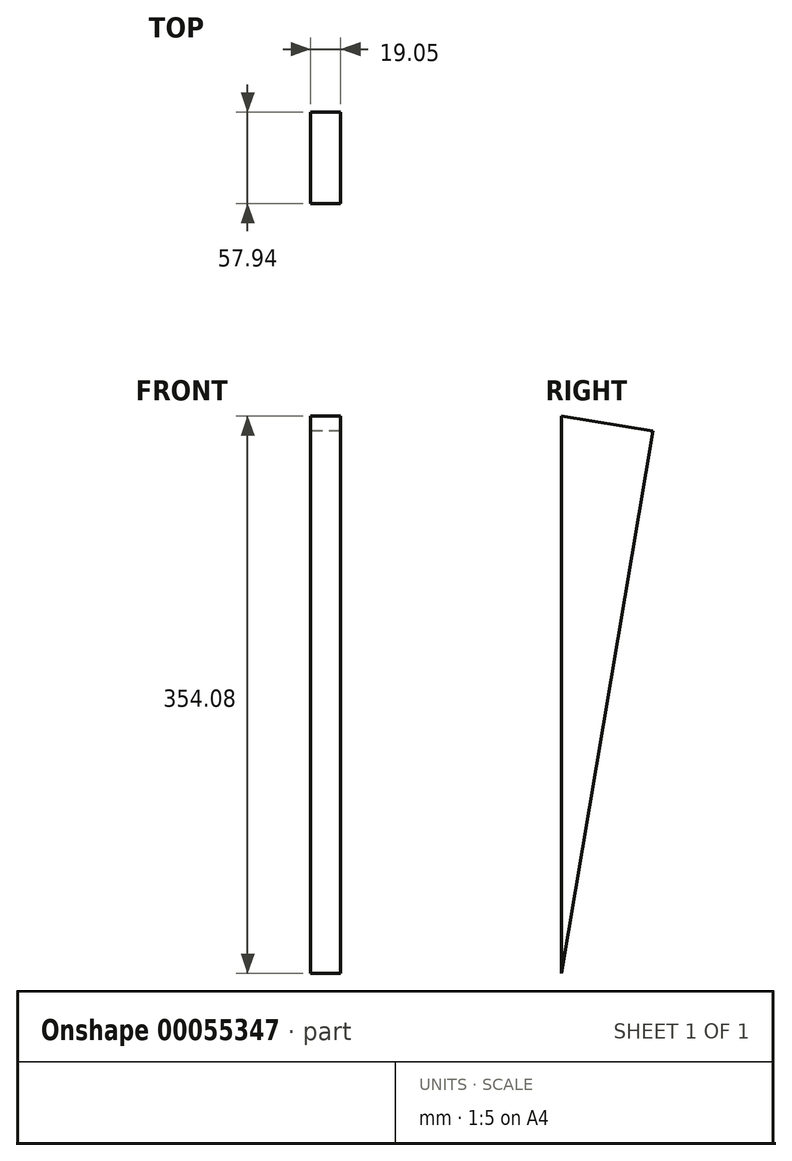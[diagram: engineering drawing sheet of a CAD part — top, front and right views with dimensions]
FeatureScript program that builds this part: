
annotation { "Feature Type Name" : "Feature", "Feature Type Description" : "" }
export const myFeature = defineFeature(function(context is Context, id is Id, definition is map)
    precondition{}
    {
        {
            var Q0;
            Q0=qCreatedBy(makeId("Right.planeOp"),FACE);
            var sketch = newSketch(context, id + "F0", { "sketchPlane" : qUnion([Q0])});
            skLineSegment(sketch, "E0", {"start": v(0, 0) * mm, "end": v(0, 354.08) * mm});
            skLineSegment(sketch, "E1", {"start": v(0, 0) * mm, "end": v(57.94, 344.41) * mm});
            skLineSegment(sketch, "E2", {"start": v(57.94, 344.41) * mm, "end": v(0, 354.08) * mm});
            skSolve(sketch);
        }
        {
            var Q0;
            Q0=qSketchRegion(id+"F0",true);
            extrude(context, id + "F1", {"entities" : qUnion([Q0]), "depth" : 19.05 * mm});
        }
    });
